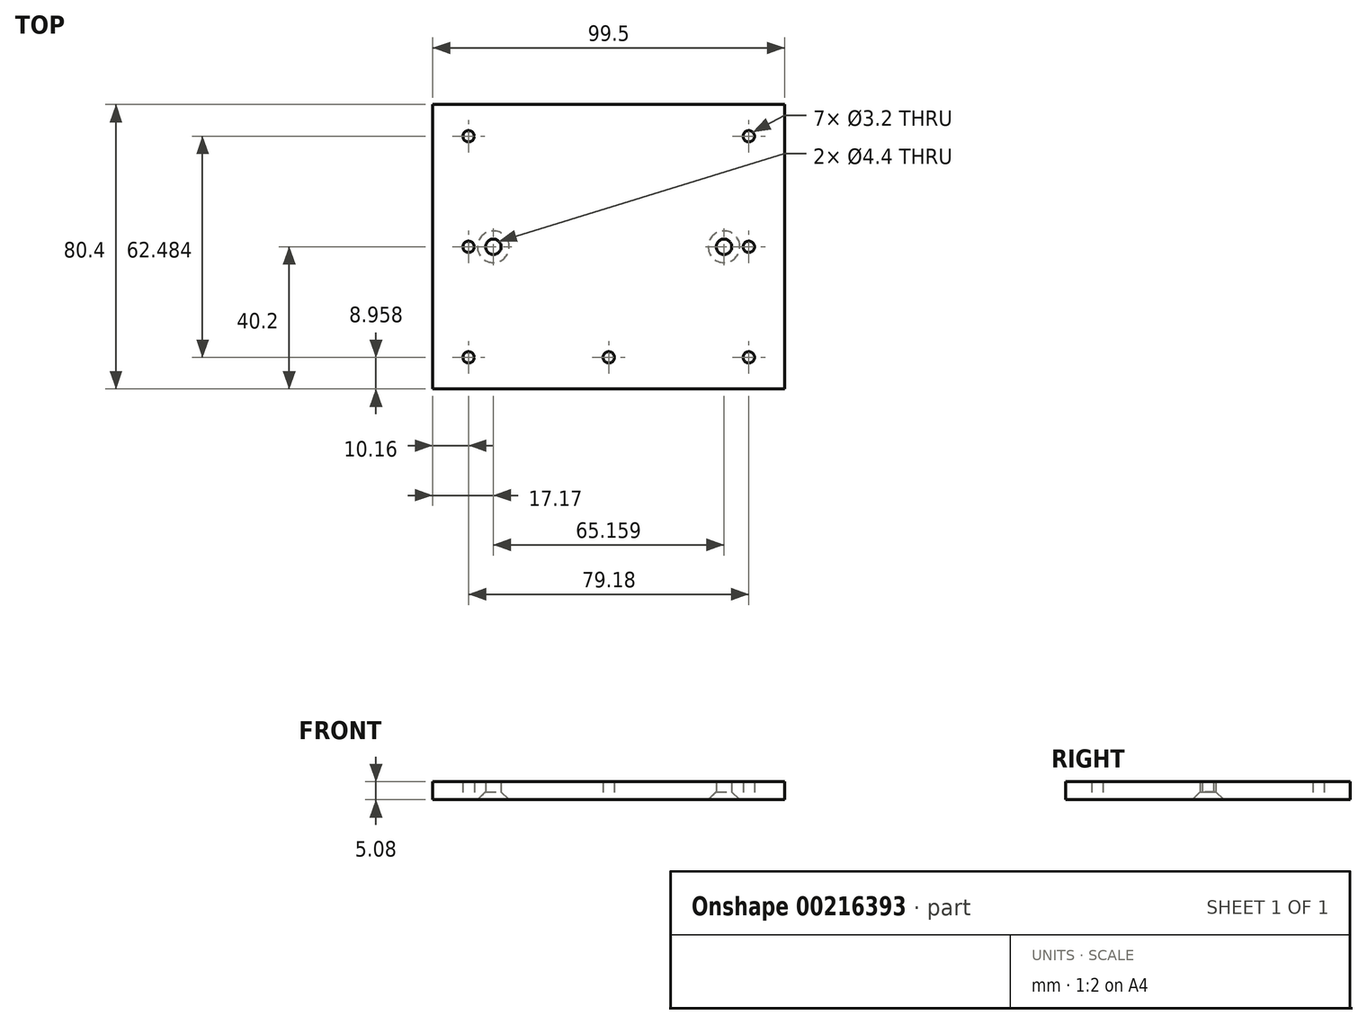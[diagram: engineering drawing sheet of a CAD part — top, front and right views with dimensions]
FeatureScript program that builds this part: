
annotation { "Feature Type Name" : "Feature", "Feature Type Description" : "" }
export const myFeature = defineFeature(function(context is Context, id is Id, definition is map)
    precondition{}
    {
        {
            var Q0;
            Q0=qCreatedBy(makeId("Top.planeOp"),FACE);
            var sketch = newSketch(context, id + "F0", { "sketchPlane" : qUnion([Q0])});
            skLineSegment(sketch, "E0.bottom", {"start": v(-49.75, -40.2) * mm, "end": v(49.75, -40.2) * mm});
            skLineSegment(sketch, "E0.top", {"start": v(-49.75, 40.2) * mm, "end": v(49.75, 40.2) * mm});
            skLineSegment(sketch, "E0.left", {"start": v(-49.75, -40.2) * mm, "end": v(-49.75, 40.2) * mm});
            skLineSegment(sketch, "E0.right", {"start": v(49.75, -40.2) * mm, "end": v(49.75, 40.2) * mm});
            skPoint(sketch, "E0.middle", {"position": v(0, 0) * mm});
            skSolve(sketch);
        }
        {
            var Q0;
            Q0 = qSketchRegion(id + "F0", true);
            extrude(context, id + "F1", {"entities" : qUnion([Q0]), "depth" : 5.08 * mm});
        }
        {
            var Q0;
            Q0=makeQuery(id+"F1.opExtrude","CAP_FACE",FACE,{"disambiguationData":[OSD([sQuery(id+"F0.wireOp",EDGE,"E0.bottom"),sQuery(id+"F0.wireOp",EDGE,"E0.top"),sQuery(id+"F0.wireOp",EDGE,"E0.left"),sQuery(id+"F0.wireOp",EDGE,"E0.right")])],"isStart":true});
            var sketch = newSketch(context, id + "F2", { "sketchPlane" : qUnion([Q0])});
            skPoint(sketch, "E1", {"position": v(-32.58, 0) * mm});
            skPoint(sketch, "E2", {"position": v(32.58, 0) * mm});
            skSolve(sketch);
        }
        {
            var Q0;
            Q0=sQuery(id+"F2.wireOp",VERTEX,"E1");
            var Q1;
            Q1=sQuery(id+"F2.wireOp",VERTEX,"E2");
            var Q2;
            Q2=makeQuery(id+"F1.opExtrude","SWEPT_BODY",BODY,{"disambiguationData":[OSD([sQuery(id+"F0.wireOp",EDGE,"E0.bottom"),sQuery(id+"F0.wireOp",EDGE,"E0.top"),sQuery(id+"F0.wireOp",EDGE,"E0.left"),sQuery(id+"F0.wireOp",EDGE,"E0.right")])]});
            hole(context, id + "F3", {"style" : HoleStyle.C_SINK, "endStyle" : HoleEndStyle.BLIND, "standardTappedOrClearance" : lookupTablePath({ "standard" : "ISO", "fit" : "Normal", "size" : "M4", "type" : "Clearance" }), "standardBlindInLast" : lookupTablePath({ "fit" : "Standard", "standard" : "ISO", "size" : "M4", "type" : "Clearance" }), "holeDiameter" : 4.4 * mm, "cSinkDiameter" : 8.96 * mm, "cSinkAngle" : 90 * degree, "holeDepth" : 38.1 * mm, "tappedDepth" : 34.92 * mm, "tapClearance" : 3, "locations" : qUnion([Q0, Q1]), "scope" : qUnion([Q2])});
        }
        {
            var Q0;
            Q0=makeQuery(id+"F1.opExtrude","CAP_FACE",FACE,{"disambiguationData":[OSD([sQuery(id+"F0.wireOp",EDGE,"E0.bottom"),sQuery(id+"F0.wireOp",EDGE,"E0.top"),sQuery(id+"F0.wireOp",EDGE,"E0.left"),sQuery(id+"F0.wireOp",EDGE,"E0.right")])],"isStart":true});
            var sketch = newSketch(context, id + "F4", { "sketchPlane" : qUnion([Q0])});
            skPoint(sketch, "E3", {"position": v(-39.6, 31.24) * mm});
            skPoint(sketch, "E4", {"position": v(-39.6, 0) * mm});
            skPoint(sketch, "E5", {"position": v(-39.6, -31.24) * mm});
            skPoint(sketch, "E6", {"position": v(39.6, 0) * mm});
            skPoint(sketch, "E7", {"position": v(39.6, -31.24) * mm});
            skPoint(sketch, "E8", {"position": v(39.6, 31.24) * mm});
            skPoint(sketch, "E9", {"position": v(-49.75, 0) * mm});
            skPoint(sketch, "E10", {"position": v(0, 31.24) * mm});
            skSolve(sketch);
        }
        {
            var Q0;
            Q0=sQuery(id+"F4.wireOp",VERTEX,"E3");
            var Q1;
            Q1=sQuery(id+"F4.wireOp",VERTEX,"E4");
            var Q2;
            Q2=sQuery(id+"F4.wireOp",VERTEX,"E5");
            var Q3;
            Q3=sQuery(id+"F4.wireOp",VERTEX,"E7");
            var Q4;
            Q4=sQuery(id+"F4.wireOp",VERTEX,"E6");
            var Q5;
            Q5=sQuery(id+"F4.wireOp",VERTEX,"E8");
            var Q6;
            Q6=sQuery(id+"F4.wireOp",VERTEX,"a43d1f21-3863-4374-9850-ad290bff0b31");
            var Q7;
            Q7=sQuery(id+"F4.wireOp",VERTEX,"E10");
            var Q8;
            Q8=makeQuery(id+"F1.opExtrude","SWEPT_BODY",BODY,{"disambiguationData":[OSD([sQuery(id+"F0.wireOp",EDGE,"E0.bottom"),sQuery(id+"F0.wireOp",EDGE,"E0.top"),sQuery(id+"F0.wireOp",EDGE,"E0.left"),sQuery(id+"F0.wireOp",EDGE,"E0.right")])]});
            hole(context, id + "F5", {"style" : HoleStyle.SIMPLE, "endStyle" : HoleEndStyle.BLIND, "standardTappedOrClearance" : lookupTablePath({ "standard" : "ISO", "engagement" : "75%", "pitch" : "0.75 mm", "size" : "M4", "type" : "Tapped" }), "standardBlindInLast" : lookupTablePath({ "standard" : "ISO", "engagement" : "75%", "pitch" : "0.75 mm", "size" : "M4", "type" : "Tapped" }), "holeDiameter" : 3.2 * mm, "showTappedDepth" : true, "holeDepth" : 37.17 * mm, "tappedDepth" : 34.92 * mm, "tapClearance" : 3, "locations" : qUnion([Q0, Q1, Q2, Q3, Q4, Q5, Q6, Q7]), "scope" : qUnion([Q8])});
        }
    });
